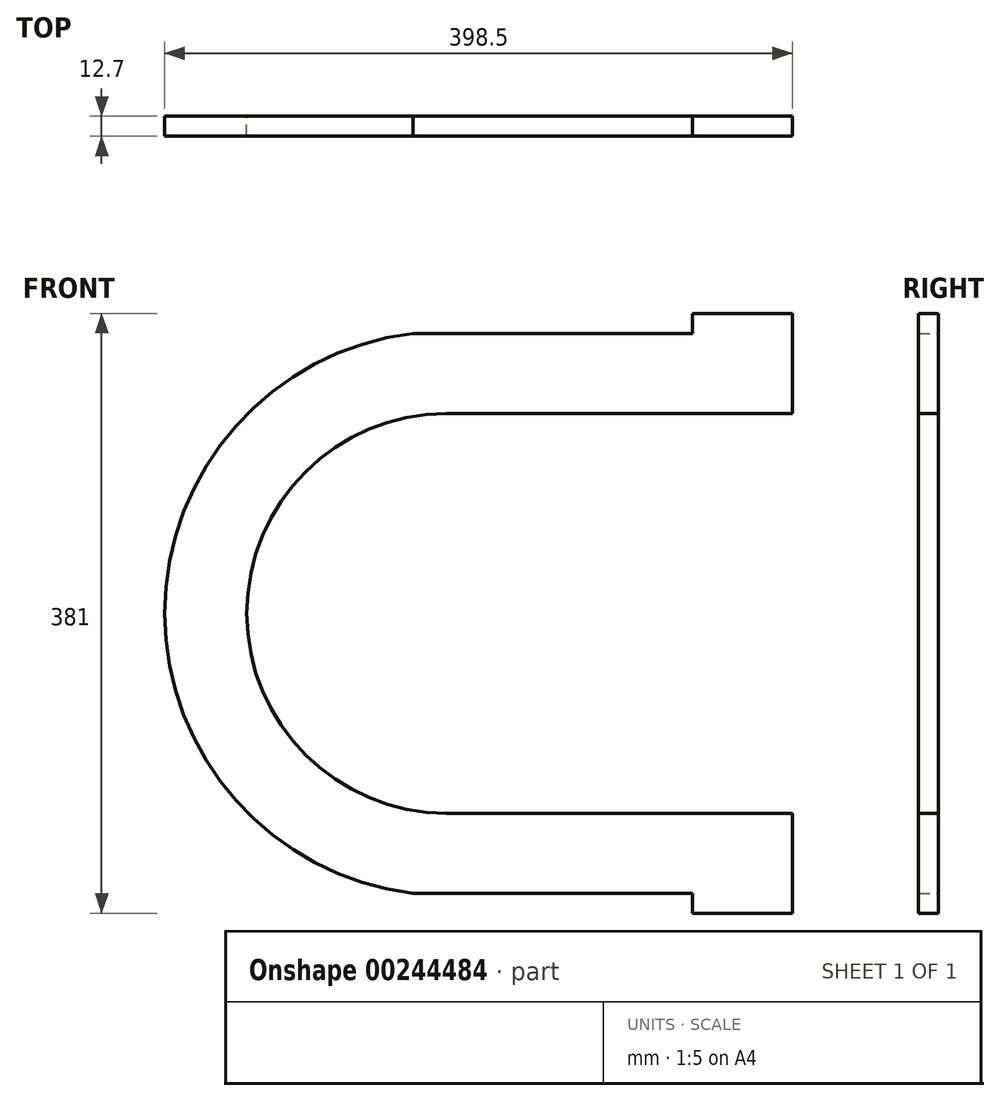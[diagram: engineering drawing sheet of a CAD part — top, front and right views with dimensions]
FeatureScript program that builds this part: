
annotation { "Feature Type Name" : "Feature", "Feature Type Description" : "" }
export const myFeature = defineFeature(function(context is Context, id is Id, definition is map)
    precondition{}
    {
        {
            var Q0;
            Q0=qCreatedBy(makeId("Front.planeOp"),FACE);
            var sketch = newSketch(context, id + "F0", { "sketchPlane" : qUnion([Q0])});
            skLineSegment(sketch, "E0.bottom", {"start": v(155.93, 177.8) * mm, "end": v(-21.29, 177.8) * mm});
            skLineSegment(sketch, "E0.top", {"start": v(155.93, -177.8) * mm, "end": v(-21.29, -177.8) * mm});
            skPoint(sketch, "E0.middle", {"position": v(0, 0) * mm});
            skArc(sketch, "E1", {"start": v(0, 127) * mm, "mid": v(-127, 0) * mm, "end": v(0, -127) * mm});
            skPoint(sketch, "E2.endSnap0", {"position": v(190.5, 0) * mm});
            skPoint(sketch, "E2.end.orphan", {"position": v(190.5, 152.4) * mm});
            skLineSegment(sketch, "E3", {"start": v(0, 127) * mm, "end": v(190.5, 127) * mm});
            skArc(sketch, "E4", {"start": v(-21.29, 177.8) * mm, "mid": v(-179.07, 0) * mm, "end": v(-21.29, -177.8) * mm});
            skLineSegment(sketch, "E5", {"start": v(0, -127) * mm, "end": v(190.5, -127) * mm});
            skPoint(sketch, "E0.right.start.orphan", {"position": v(-190.5, 177.8) * mm});
            skPoint(sketch, "E6.orphan", {"position": v(-190.5, -177.8) * mm});
            skLineSegment(sketch, "E7.bottom", {"start": v(155.93, 127) * mm, "end": v(219.43, 127) * mm});
            skLineSegment(sketch, "E7.top", {"start": v(155.93, 190.5) * mm, "end": v(219.43, 190.5) * mm});
            skLineSegment(sketch, "E7.left", {"start": v(155.93, 177.8) * mm, "end": v(155.93, 190.5) * mm});
            skLineSegment(sketch, "E7.right", {"start": v(219.43, 127) * mm, "end": v(219.43, 190.5) * mm});
            skLineSegment(sketch, "E8.bottom", {"start": v(155.93, -127) * mm, "end": v(219.43, -127) * mm});
            skLineSegment(sketch, "E8.top", {"start": v(155.93, -190.5) * mm, "end": v(219.43, -190.5) * mm});
            skLineSegment(sketch, "E8.left", {"start": v(155.93, -177.8) * mm, "end": v(155.93, -190.5) * mm});
            skLineSegment(sketch, "E8.right", {"start": v(219.43, -127) * mm, "end": v(219.43, -190.5) * mm});
            skPoint(sketch, "E9.trimOffspring.end.orphan", {"position": v(190.5, -177.8) * mm});
            skPoint(sketch, "E10.orphan", {"position": v(190.5, 177.8) * mm});
            skSolve(sketch);
        }
        {
            var Q0;
            Q0=makeQuery(id+"F0.imprint","IMPRINT",FACE,{"disambiguationData":[TD([[makeQuery(id+"F0.imprint","IMPRINT",EDGE,{"derivedFrom":sQuery(id+"F0.wireOp",EDGE,"E0.bottom")}),1.0]])]});
            extrude(context, id + "F1", {"entities" : qUnion([Q0]), "depth" : 12.7 * mm});
        }
    });
